# Revit family: EDFPVR214C
name_source: partatom
category: Plumbing Fixtures
units: mm (PartAtom-declared; Revit-internal decimal feet)

## family parameters
Always vertical = Yes
Cut with Voids When Loaded = No
Part Type = Normal
Room Calculation Point = No
Round Connector Dimension = Use Diameter
Shared = No
Work Plane-Based = No

## types (1)
- EDFPVR214C
    Activation by = Mechanical Front Bubbler Button
    Approx. Shipping Weight = 20 lbs.
    Bubbler Style = Vandal Resistant
    Chilling Capacity = Non-refrigerated
    Description = Elkay Soft Sides Single Fountain Non-Filtered Non-Refrigerated
Stainless
    Dimensions (L x W x H) = 12-1/8 inch  x 18-3/4 inch x 6-1/2 inch
    Finish = Stainless Steel
    Installation Location = Indoor + Outdoor
    Manufacturer = ELKAY
    Model = EDFPVR214C
    Mounting Type = Wall Mount (On Wall)
    Number of Stations = 1
    Power = No Electrical Required
    Version = 1.0.0.0

## geometry (parser evidence)
native form markers: Sweep x3
no freeform markers — native parametric forms only
